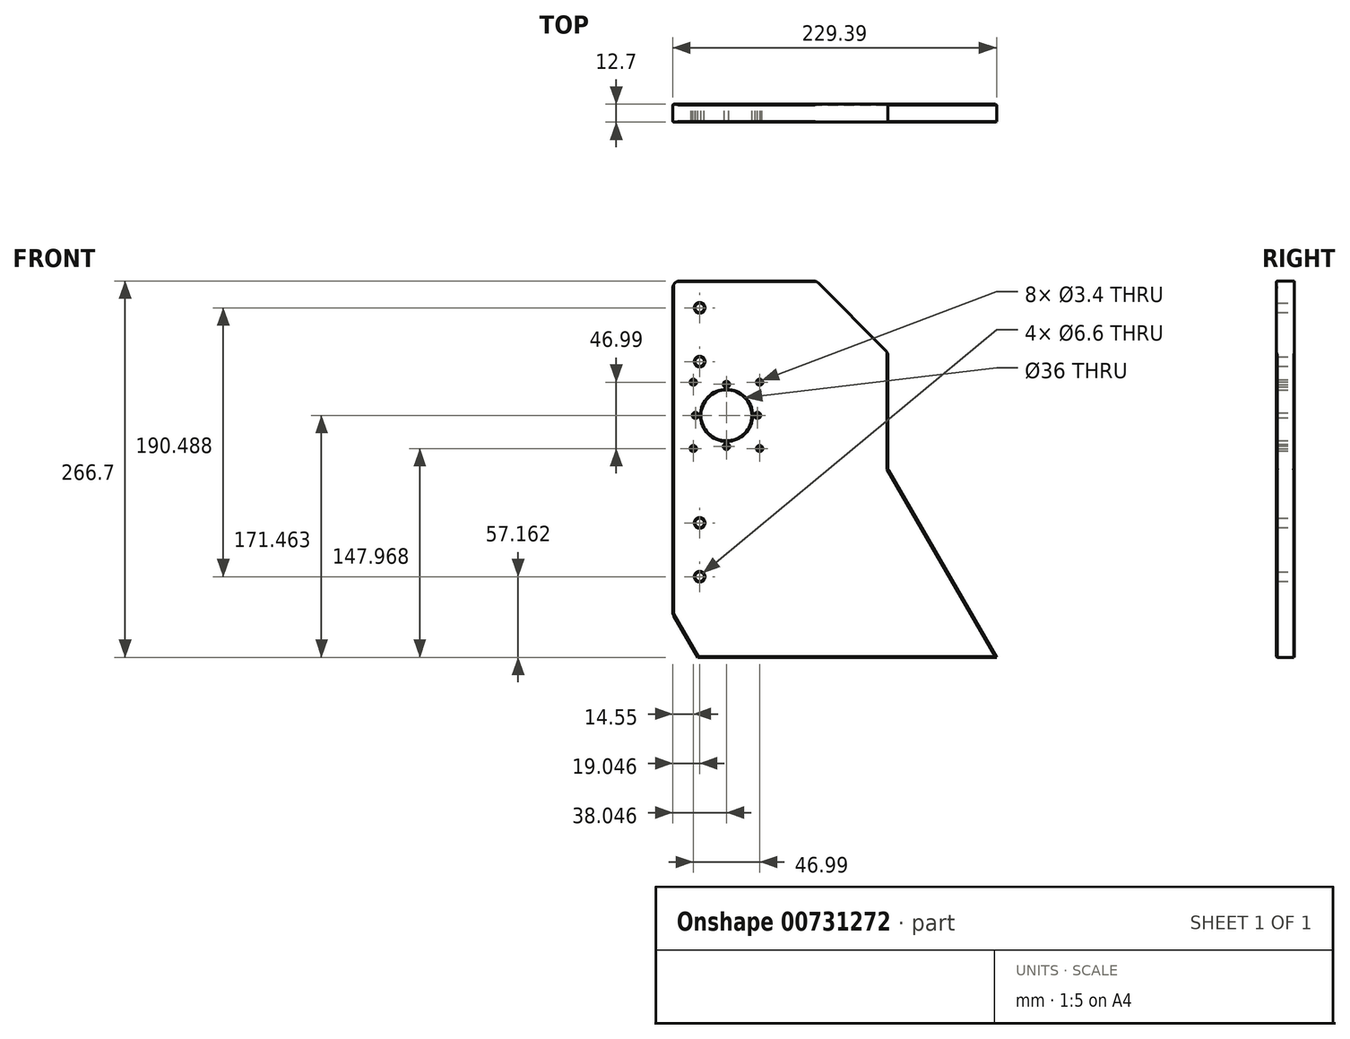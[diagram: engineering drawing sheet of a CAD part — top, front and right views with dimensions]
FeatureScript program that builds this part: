
annotation { "Feature Type Name" : "Feature", "Feature Type Description" : "" }
export const myFeature = defineFeature(function(context is Context, id is Id, definition is map)
    precondition{}
    {
        {
            var Q0;
            Q0=qCreatedBy(makeId("Front.planeOp"),FACE);
            var sketch = newSketch(context, id + "F0", { "sketchPlane" : qUnion([Q0])});
            skLineSegment(sketch, "E0.bottom", {"start": v(197.33, 133.35) * mm, "end": v(-107.47, 133.35) * mm});
            skLineSegment(sketch, "E0.left", {"start": v(197.33, 133.35) * mm, "end": v(197.33, -133.35) * mm});
            skLineSegment(sketch, "E0.right", {"start": v(-107.47, 133.35) * mm, "end": v(-107.47, -133.35) * mm});
            skPoint(sketch, "E0.middle", {"position": v(0, 0) * mm});
            skCircle(sketch, "E1", {"center": v(-88.42, -76.19) * mm, "radius": 3.3 * mm});
            skCircle(sketch, "E2", {"center": v(-88.42, -38.09) * mm, "radius": 3.3 * mm});
            skCircle(sketch, "E3", {"center": v(-88.42, 76.2) * mm, "radius": 3.3 * mm});
            skCircle(sketch, "E4", {"center": v(-88.42, 114.3) * mm, "radius": 3.3 * mm});
            skLineSegment(sketch, "E5", {"start": v(-107.47, -133.35) * mm, "end": v(197.33, -133.35) * mm});
            skPoint(sketch, "E6.middle", {"position": v(-69.42, 38.11) * mm});
            skLineSegment(sketch, "E7", {"start": v(-69.42, 74.31) * mm, "end": v(-69.42, 11.11) * mm, "construction": true});
            skPoint(sketch, "E8.startSnap0", {"position": v(44.93, 133.35) * mm});
            skCircle(sketch, "E9", {"center": v(-69.42, 38.11) * mm, "radius": 18 * mm});
            skLineSegment(sketch, "E10", {"start": v(-98.77, 38.11) * mm, "end": v(-40.23, 38.11) * mm, "construction": true});
            skLineSegment(sketch, "E11", {"start": v(-91.1, 59.79) * mm, "end": v(-42.84, 11.53) * mm, "construction": true});
            skLineSegment(sketch, "E12", {"start": v(-49.22, 58.32) * mm, "end": v(-94.15, 13.39) * mm, "construction": true});
            skCircle(sketch, "E13", {"center": v(-92.92, 61.6) * mm, "radius": 1.7 * mm});
            skCircle(sketch, "E14.MirrorC", {"center": v(-92.92, 14.62) * mm, "radius": 1.7 * mm});
            skCircle(sketch, "E15.MirrorC", {"center": v(-45.93, 61.6) * mm, "radius": 1.7 * mm});
            skCircle(sketch, "E16.MirrorC", {"center": v(-45.93, 14.62) * mm, "radius": 1.7 * mm});
            skCircle(sketch, "E17", {"center": v(-69.42, 60.11) * mm, "radius": 1.7 * mm});
            skCircle(sketch, "E18.MirrorC", {"center": v(-69.42, 16.11) * mm, "radius": 1.7 * mm});
            skCircle(sketch, "E19", {"center": v(-91.42, 38.11) * mm, "radius": 1.7 * mm});
            skCircle(sketch, "E20.MirrorC", {"center": v(-47.42, 38.11) * mm, "radius": 1.7 * mm});
            skLineSegment(sketch, "E21", {"start": v(44.93, 133.35) * mm, "end": v(44.93, 0) * mm});
            skLineSegment(sketch, "E22", {"start": v(44.93, 0) * mm, "end": v(121.92, -133.35) * mm});
            skLineSegment(sketch, "E23", {"start": v(-107.47, -102.67) * mm, "end": v(-89.76, -133.35) * mm});
            skSolve(sketch);
        }
        {
            var Q0;
            Q0=makeQuery(id+"F0.imprint","IMPRINT",FACE,{"disambiguationData":[TD([[makeQuery(id+"F0.imprint","IMPRINT",EDGE,{"derivedFrom":sQuery(id+"F0.wireOp",EDGE,"E1")}),-1.0]])]});
            extrude(context, id + "F1", {"entities" : qUnion([Q0]), "depth" : 12.7 * mm, "offsetDistance" : 25.4 * mm});
        }
        {
            var Q0;
            Q0=makeQuery(id+"F1.opExtrude","CAP_FACE",FACE,{"disambiguationData":[OSD([sQuery(id+"F0.wireOp",EDGE,"E0.bottom"),sQuery(id+"F0.wireOp",EDGE,"E0.right"),sQuery(id+"F0.wireOp",EDGE,"E1"),sQuery(id+"F0.wireOp",EDGE,"E2"),sQuery(id+"F0.wireOp",EDGE,"E3"),sQuery(id+"F0.wireOp",EDGE,"E4"),sQuery(id+"F0.wireOp",EDGE,"E5"),sQuery(id+"F0.wireOp",EDGE,"E9"),sQuery(id+"F0.wireOp",EDGE,"E13"),sQuery(id+"F0.wireOp",EDGE,"E14.MirrorC"),sQuery(id+"F0.wireOp",EDGE,"E15.MirrorC"),sQuery(id+"F0.wireOp",EDGE,"E16.MirrorC"),sQuery(id+"F0.wireOp",EDGE,"E17"),sQuery(id+"F0.wireOp",EDGE,"E18.MirrorC"),sQuery(id+"F0.wireOp",EDGE,"E19"),sQuery(id+"F0.wireOp",EDGE,"E20.MirrorC"),sQuery(id+"F0.wireOp",EDGE,"E21"),sQuery(id+"F0.wireOp",EDGE,"E22"),sQuery(id+"F0.wireOp",EDGE,"VAuwBF5W-I5Uy-UODp-YZlw-XCtFeHULHEPd")])],"isStart":false});
            var Q1;
            Q1=makeQuery(id+"F1.opExtrude","CAP_FACE",FACE,{"disambiguationData":[OSD([sQuery(id+"F0.wireOp",EDGE,"E0.bottom"),sQuery(id+"F0.wireOp",EDGE,"E0.right"),sQuery(id+"F0.wireOp",EDGE,"E1"),sQuery(id+"F0.wireOp",EDGE,"E2"),sQuery(id+"F0.wireOp",EDGE,"E3"),sQuery(id+"F0.wireOp",EDGE,"E4"),sQuery(id+"F0.wireOp",EDGE,"E5"),sQuery(id+"F0.wireOp",EDGE,"E9"),sQuery(id+"F0.wireOp",EDGE,"E13"),sQuery(id+"F0.wireOp",EDGE,"E14.MirrorC"),sQuery(id+"F0.wireOp",EDGE,"E15.MirrorC"),sQuery(id+"F0.wireOp",EDGE,"E16.MirrorC"),sQuery(id+"F0.wireOp",EDGE,"E17"),sQuery(id+"F0.wireOp",EDGE,"E18.MirrorC"),sQuery(id+"F0.wireOp",EDGE,"E19"),sQuery(id+"F0.wireOp",EDGE,"E20.MirrorC"),sQuery(id+"F0.wireOp",EDGE,"E21"),sQuery(id+"F0.wireOp",EDGE,"E22"),sQuery(id+"F0.wireOp",EDGE,"VAuwBF5W-I5Uy-UODp-YZlw-XCtFeHULHEPd")])],"isStart":true});
            chamfer(context, id + "F2", {"entities" : qUnion([Q0, Q1]), "width" : 0.5 * mm, "tangentPropagation" : true});
        }
        {
            var Q0;
            Q0=makeQuery(id+"F1.opExtrude","SWEPT_EDGE",EDGE,{"disambiguationData":[OSD([sQuery(id+"F0.wireOp",EDGE,"E0.bottom"),sQuery(id+"F0.wireOp",EDGE,"E21")])]});
            chamfer(context, id + "F3", {"entities" : qUnion([Q0]), "width" : 50.8 * mm, "tangentPropagation" : true});
        }
        {
            var Q0;
            {var subQ0=sQuery(id+"F0.wireOp",EDGE,"E21");Q0=makeQuery(id+"F3.opChamfer","BLEND_EDGE",EDGE,{"blendedFrom":[makeQuery(id+"F1.opExtrude","SWEPT_EDGE",EDGE,{"disambiguationData":[OSD([sQuery(id+"F0.wireOp",EDGE,"E0.bottom"),subQ0])]}),makeQuery(id+"F1.opExtrude","SWEPT_FACE",FACE,{"disambiguationData":[OSD([subQ0])]})],"blendedInto":[makeQuery(id+"F1.opExtrude","SWEPT_FACE",FACE,{"disambiguationData":[OSD([subQ0])]})]});}
            var Q1;
            Q1=makeQuery(id+"F1.opExtrude","SWEPT_EDGE",EDGE,{"disambiguationData":[OSD([sQuery(id+"F0.wireOp",EDGE,"E21"),sQuery(id+"F0.wireOp",EDGE,"E22")])]});
            var Q2;
            Q2=makeQuery(id+"F1.opExtrude","SWEPT_EDGE",EDGE,{"disambiguationData":[OSD([sQuery(id+"F0.wireOp",EDGE,"E0.right"),sQuery(id+"F0.wireOp",EDGE,"E23")])]});
            var Q3;
            Q3=makeQuery(id+"F1.opExtrude","SWEPT_EDGE",EDGE,{"disambiguationData":[OSD([sQuery(id+"F0.wireOp",EDGE,"E0.bottom"),sQuery(id+"F0.wireOp",EDGE,"E0.right")])]});
            var Q4;
            {var subQ0=sQuery(id+"F0.wireOp",EDGE,"E0.bottom");Q4=makeQuery(id+"F3.opChamfer","BLEND_EDGE",EDGE,{"blendedFrom":[makeQuery(id+"F1.opExtrude","SWEPT_EDGE",EDGE,{"disambiguationData":[OSD([subQ0,sQuery(id+"F0.wireOp",EDGE,"E21")])]}),makeQuery(id+"F1.opExtrude","SWEPT_FACE",FACE,{"disambiguationData":[OSD([subQ0])]})],"blendedInto":[makeQuery(id+"F1.opExtrude","SWEPT_FACE",FACE,{"disambiguationData":[OSD([subQ0])]})]});}
            fillet(context, id + "F4", {"entities" : qUnion([Q0, Q1, Q2, Q3, Q4]), "radius" : 5.08 * mm, "tangentPropagation" : true, "allowEdgeOverflow" : false});
        }
    });
